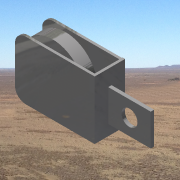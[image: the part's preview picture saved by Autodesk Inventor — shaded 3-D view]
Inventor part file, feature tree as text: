
AUTODESK INVENTOR PART (.ipt)
format: ipt  version: 2013 SP2 (Build 170200200, 200)  size: 183,808 bytes
history: native  units: in
note: dims shown in document units (in); Inventor stores cm internally (conversion verified against a paired STEP export)
features: extrude x6, sketch x6, plane x1, mirror x1
ambient origin geometry x8: Origin, YZ Plane, XZ Plane, XY Plane, X Axis, Y Axis, Z Axis, Center Point
bodies: Solid1 (feature_tree)
feature tree (14):
  extrude  "wheel"  Depth=0.3in TaperAngle=0.0deg
  extrude  "axle"  Depth=0.2in TaperAngle=0.0deg
  extrude  "side"  Depth=0.25in
  plane  "Work Plane1"
  mirror  "Mirror1"
  extrude  "Extrusion4"  Depth=0.06in TaperAngle=0.0deg
  extrude  "Extrusion5"  Depth=0.5in
  extrude  "Extrusion6"  [1 undecoded]
  sketch  "Sketch1"  dims[d0=1.5in d2=0.3in d3=0.0in]
  sketch  "Sketch2"  dims[d4=0.3in d7=0.2in d8=0.5in d9=0.0in d10=0.0in]
  sketch  "Sketch3"  dims[d11=0.06in d12=0.0in d13=0.25in]
  sketch  "Sketch4"  dims[d14=-0.35in d15=0.06in d16=0.0in]
  sketch  "Sketch5"  dims[d17=1.0in d18=0.0in d19=0.5in]
  sketch  "Sketch6"  dims[d20=1.0in d21=0.0in]
note: 1 required parameter value undecoded (feature->parameter linkage not recoverable at this tier; creation-order binding heuristic only, values carry confidence <= 0.55)
